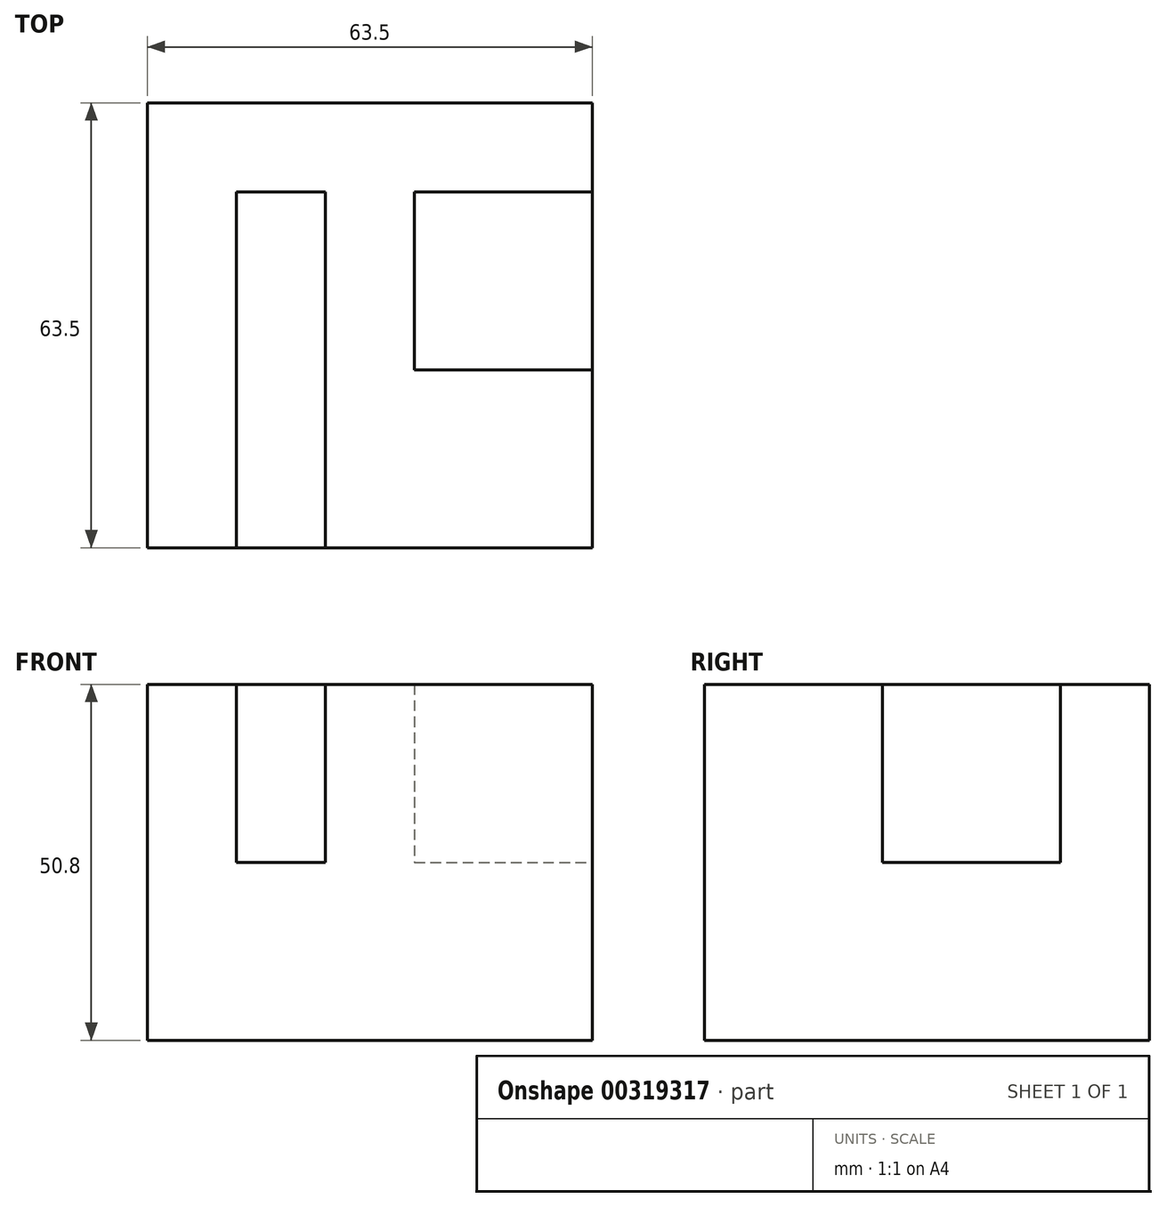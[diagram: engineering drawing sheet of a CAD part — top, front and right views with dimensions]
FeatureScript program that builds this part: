
annotation { "Feature Type Name" : "Feature", "Feature Type Description" : "" }
export const myFeature = defineFeature(function(context is Context, id is Id, definition is map)
    precondition{}
    {
        {
            var Q0;
            Q0=qCreatedBy(makeId("Top.planeOp"),FACE);
            var sketch = newSketch(context, id + "F0", { "sketchPlane" : qUnion([Q0])});
            skLineSegment(sketch, "E0", {"start": v(-36.24, -32.51) * mm, "end": v(27.26, -32.51) * mm});
            skLineSegment(sketch, "E1", {"start": v(27.26, -32.51) * mm, "end": v(27.26, 30.99) * mm});
            skLineSegment(sketch, "E2", {"start": v(27.26, 30.99) * mm, "end": v(-36.24, 30.99) * mm});
            skLineSegment(sketch, "E3", {"start": v(-36.24, 30.99) * mm, "end": v(-36.24, -32.51) * mm});
            skSolve(sketch);
        }
        {
            var Q0;
            Q0=makeQuery(id+"F0.imprint","IMPRINT",FACE,{"disambiguationData":[TD([[makeQuery(id+"F0.imprint","IMPRINT",EDGE,{"derivedFrom":sQuery(id+"F0.wireOp",EDGE,"E0")}),1.0]])]});
            extrude(context, id + "F1", {"entities" : qUnion([Q0]), "depth" : 25.4 * mm});
        }
        {
            var Q0;
            Q0=makeQuery(id+"F1.opExtrude","CAP_FACE",FACE,{"disambiguationData":[OSD([sQuery(id+"F0.wireOp",EDGE,"E0"),sQuery(id+"F0.wireOp",EDGE,"E1"),sQuery(id+"F0.wireOp",EDGE,"E2"),sQuery(id+"F0.wireOp",EDGE,"E3")])],"isStart":false});
            var sketch = newSketch(context, id + "F2", { "sketchPlane" : qUnion([Q0])});
            skLineSegment(sketch, "E4", {"start": v(-36.24, -32.51) * mm, "end": v(-23.54, -32.51) * mm});
            skLineSegment(sketch, "E5", {"start": v(-23.54, -32.51) * mm, "end": v(-23.54, 18.29) * mm});
            skLineSegment(sketch, "E6", {"start": v(-23.54, 18.29) * mm, "end": v(-10.84, 18.29) * mm});
            skLineSegment(sketch, "E7", {"start": v(-10.84, 18.29) * mm, "end": v(-10.84, -32.51) * mm});
            skLineSegment(sketch, "E8", {"start": v(-10.84, -32.51) * mm, "end": v(27.26, -32.51) * mm});
            skLineSegment(sketch, "E9", {"start": v(27.26, -32.51) * mm, "end": v(27.26, -7.11) * mm});
            skLineSegment(sketch, "E10", {"start": v(27.26, -7.11) * mm, "end": v(1.86, -7.11) * mm});
            skLineSegment(sketch, "E11", {"start": v(1.86, -7.11) * mm, "end": v(1.86, 18.29) * mm});
            skLineSegment(sketch, "E12", {"start": v(1.86, 18.29) * mm, "end": v(27.26, 18.29) * mm});
            skLineSegment(sketch, "E13", {"start": v(27.26, 18.29) * mm, "end": v(27.26, 30.99) * mm});
            skLineSegment(sketch, "E14", {"start": v(27.26, 30.99) * mm, "end": v(-36.24, 30.99) * mm});
            skLineSegment(sketch, "E15", {"start": v(-36.24, 30.99) * mm, "end": v(-36.24, -32.51) * mm});
            skSolve(sketch);
        }
        {
            var Q0;
            Q0=makeQuery(id+"F2.imprint","IMPRINT",FACE,{"disambiguationData":[TD([[makeQuery(id+"F2.imprint","IMPRINT",EDGE,{"derivedFrom":sQuery(id+"F2.wireOp",EDGE,"E4")}),1.0]])]});
            extrude(context, id + "F3", {"entities" : qUnion([Q0]), "operationType" : NewBodyOperationType.ADD, "depth" : 25.4 * mm});
        }
    });
